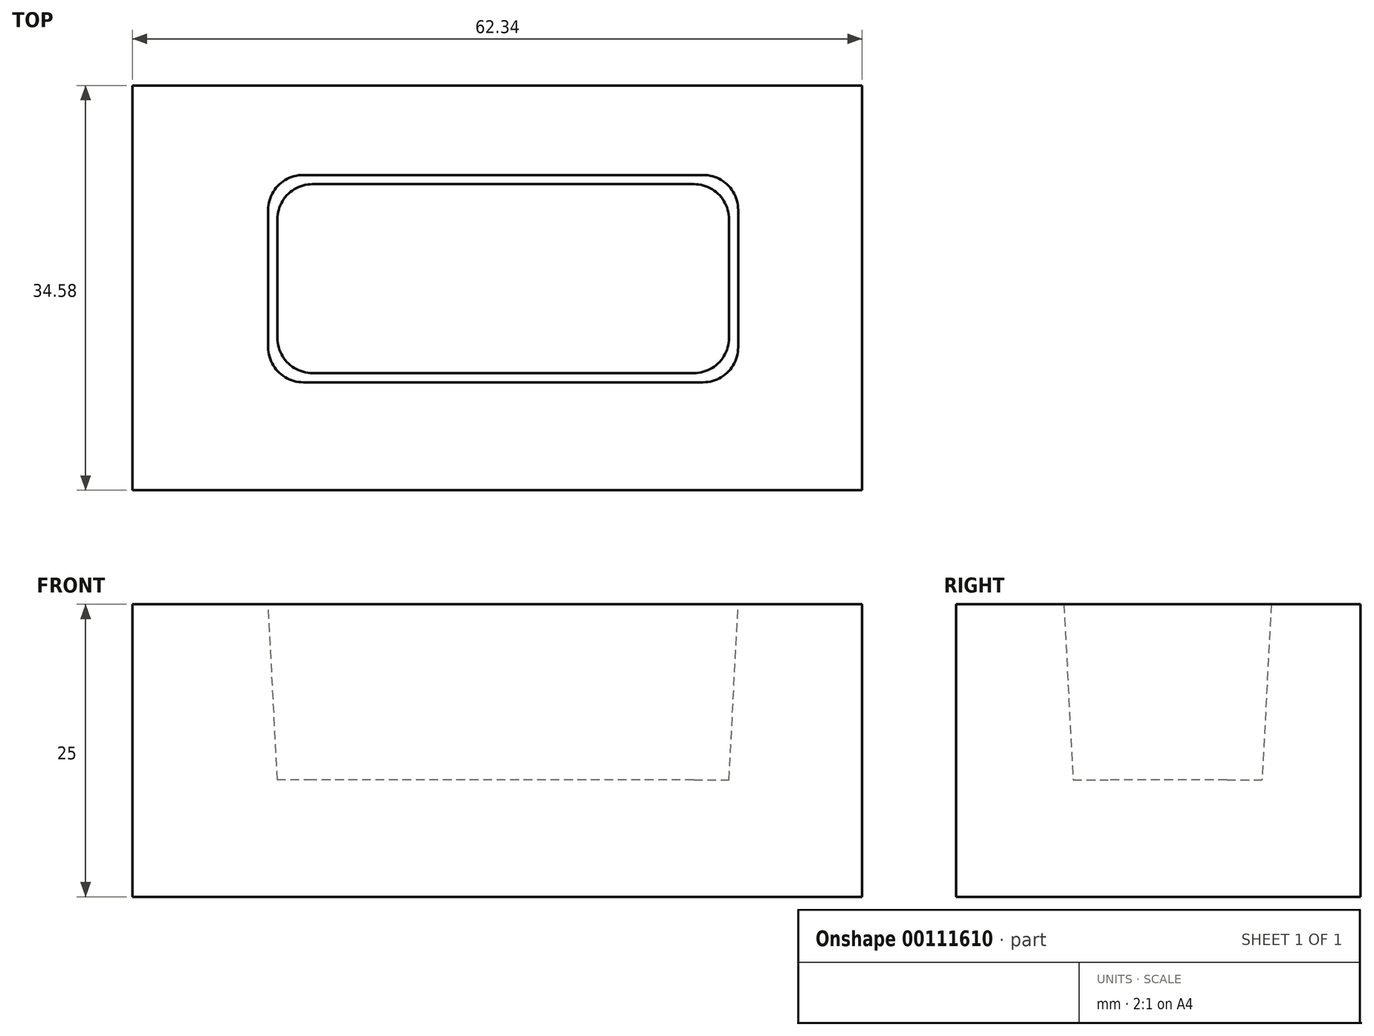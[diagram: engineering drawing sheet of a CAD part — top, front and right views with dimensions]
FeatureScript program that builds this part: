
annotation { "Feature Type Name" : "Feature", "Feature Type Description" : "" }
export const myFeature = defineFeature(function(context is Context, id is Id, definition is map)
    precondition{}
    {
        {
            var Q0;
            Q0=qCreatedBy(makeId("Top.planeOp"),FACE);
            var sketch = newSketch(context, id + "F0", { "sketchPlane" : qUnion([Q0])});
            skLineSegment(sketch, "E0.bottom", {"start": v(-31.17, 17.1) * mm, "end": v(31.17, 17.1) * mm});
            skLineSegment(sketch, "E0.top", {"start": v(-31.17, -17.48) * mm, "end": v(31.17, -17.48) * mm});
            skLineSegment(sketch, "E0.left", {"start": v(-31.17, 17.1) * mm, "end": v(-31.17, -17.48) * mm});
            skLineSegment(sketch, "E0.right", {"start": v(31.17, 17.1) * mm, "end": v(31.17, -17.48) * mm});
            skSolve(sketch);
        }
        {
            var Q0;
            Q0 = qSketchRegion(id + "F0", true);
            extrude(context, id + "F1", {"entities" : qUnion([Q0]), "oppositeDirection" : true, "depth" : 25 * mm});
        }
        {
            var Q0;
            Q0=makeQuery(id+"F1.opExtrude","CAP_FACE",FACE,{"disambiguationData":[OSD([sQuery(id+"F0.wireOp",EDGE,"E0.bottom"),sQuery(id+"F0.wireOp",EDGE,"E0.top"),sQuery(id+"F0.wireOp",EDGE,"E0.left"),sQuery(id+"F0.wireOp",EDGE,"E0.right")])],"isStart":true});
            var sketch = newSketch(context, id + "F2", { "sketchPlane" : qUnion([Q0])});
            skLineSegment(sketch, "E1.bottom", {"start": v(-19.57, 9.46) * mm, "end": v(20.57, 9.46) * mm});
            skLineSegment(sketch, "E1.top", {"start": v(-19.57, -8.25) * mm, "end": v(20.57, -8.25) * mm});
            skLineSegment(sketch, "E1.left", {"start": v(-19.57, 9.46) * mm, "end": v(-19.57, -8.25) * mm});
            skLineSegment(sketch, "E1.right", {"start": v(20.57, 9.46) * mm, "end": v(20.57, -8.25) * mm});
            skSolve(sketch);
        }
        {
            var Q0;
            Q0 = qSketchRegion(id + "F2", true);
            extrude(context, id + "F3", {"entities" : qUnion([Q0]), "operationType" : NewBodyOperationType.REMOVE, "oppositeDirection" : true, "depth" : 15 * mm, "hasDraft" : true, "draftAngle" : 3 * degree, "draftPullDirection" : true});
        }
        {
            var Q0;
            Q0=makeQuery(id+"F3.boolean.opBoolean","COPY",EDGE,{"derivedFrom":makeQuery(id+"F3.opExtrude","SWEPT_EDGE",EDGE,{"disambiguationData":[OSD([sQuery(id+"F2.wireOp",EDGE,"E1.bottom"),sQuery(id+"F2.wireOp",EDGE,"E1.left")])]})});
            var Q1;
            Q1=makeQuery(id+"F3.boolean.opBoolean","COPY",EDGE,{"derivedFrom":makeQuery(id+"F3.opExtrude","SWEPT_EDGE",EDGE,{"disambiguationData":[OSD([sQuery(id+"F2.wireOp",EDGE,"E1.top"),sQuery(id+"F2.wireOp",EDGE,"E1.left")])]})});
            var Q2;
            Q2=makeQuery(id+"F3.boolean.opBoolean","COPY",EDGE,{"derivedFrom":makeQuery(id+"F3.opExtrude","SWEPT_EDGE",EDGE,{"disambiguationData":[OSD([sQuery(id+"F2.wireOp",EDGE,"E1.bottom"),sQuery(id+"F2.wireOp",EDGE,"E1.right")])]})});
            var Q3;
            Q3=makeQuery(id+"F3.boolean.opBoolean","COPY",EDGE,{"derivedFrom":makeQuery(id+"F3.opExtrude","SWEPT_EDGE",EDGE,{"disambiguationData":[OSD([sQuery(id+"F2.wireOp",EDGE,"E1.top"),sQuery(id+"F2.wireOp",EDGE,"E1.right")])]})});
            fillet(context, id + "F4", {"entities" : qUnion([Q0, Q1, Q2, Q3]), "radius" : 3 * mm, "tangentPropagation" : true, "allowEdgeOverflow" : false});
        }
    });
